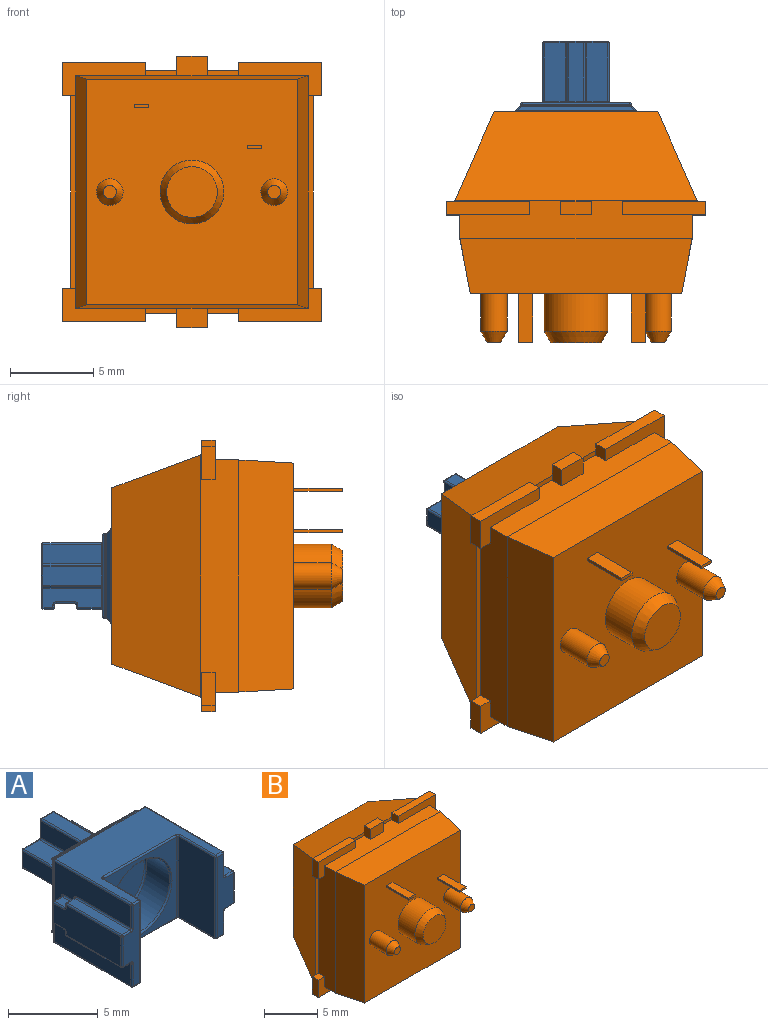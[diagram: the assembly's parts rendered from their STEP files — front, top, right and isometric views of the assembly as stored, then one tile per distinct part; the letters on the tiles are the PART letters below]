
ASSEMBLY  parts=2 mates=1
PART A: 279 faces, bbox 8.9x10.4x5.7 mm
  f0: plane 7.1x6.06mm, normal (0,0,1), area 24.7mm2, adj f124,f129,f136,f137,f148,f155,f161,f168
  f1: plane 3.5x1.15mm, normal (1,0,0), area 3.5mm2, adj f228,f239,f240,f248,f249,f263,f264,f273
  f2: plane 1.4x0.9mm, normal (0,0,-1), area 1.3mm2, adj f250,f251,f264,f265
  f3: plane 0.9x0.6mm, normal (0,0,-1), area 0.5mm2, adj f246,f247,f262,f263
  f4: plane 3.5x1.15mm, normal (-1,0,0), area 3.5mm2, adj f219,f220,f225,f226,f230,f232,f245,f246
  f5: plane 6.06x5.5mm, normal (-1,0,0), area 20.6mm2, adj f61,f68,f69,f79,f88,f89,f100,f112
  f6: plane 5.7x5.5mm, normal (0,-1,0), area 11.7mm2, adj f101,f114,f123,f124,f198
  f7: plane 6.5x4.9mm, normal (0,1,0), area 22.1mm2, adj f163,f172,f173,f174,f205,f206,f210,f211
  f8: plane 6.06x5.5mm, normal (1,0,0), area 20.6mm2, adj f63,f73,f74,f83,f93,f94,f103,f117
  f9: plane 7.1x6.06mm, normal (0,0,-1), area 24.7mm2, adj f101,f106,f107,f121,f122,f142,f143,f157
  f10: cylinder r=2.4mm len=4.8mm, axis (0,-1,0), area 27.1mm2, adj f197,f198
  f11: plane 4.6x4.6mm, normal (0,-1,0), area 16.6mm2, adj f197
  f12: plane 4.9x0.06mm, normal (1,0,0), area 0.3mm2, adj f174,f175,f191,f192
  f13: plane 6.5x0.06mm, normal (0,0,-1), area 0.4mm2, adj f163,f171,f175,f177
  f14: plane 4.9x0.06mm, normal (-1,0,0), area 0.3mm2, adj f171,f172,f189,f190
  f15: plane 6.5x0.06mm, normal (0,0,1), area 0.4mm2, adj f173,f190,f191,f196
  f16: plane 3.5x1.25mm, normal (0,0,-1), area 4.4mm2, adj f267,f272,f275,f278
  f17: plane 3.5x1.25mm, normal (0,0,-1), area 4.4mm2, adj f214,f231,f232,f233
  f18: plane 3.5x1.1mm, normal (-1,0,0), area 3.9mm2, adj f204,f213,f214,f215
  f19: plane 3.5x1.25mm, normal (0,0,1), area 4.4mm2, adj f199,f203,f204,f205
  f20: plane 3.5x1.15mm, normal (-1,0,0), area 4mm2, adj f199,f202,f206,f207
  f21: plane 3.5x0.9mm, normal (0,0,1), area 3.1mm2, adj f207,f212,f216,f217
  f22: plane 3.5x1.15mm, normal (1,0,0), area 4mm2, adj f217,f224,f234,f235
  f23: plane 3.5x1.25mm, normal (0,0,1), area 4.4mm2, adj f235,f244,f253,f254
  f24: plane 3.5x1.1mm, normal (1,0,0), area 3.9mm2, adj f254,f261,f266,f267
  f25: plane 3.8x3.8mm, normal (0,1,0), area 6.6mm2, adj f200,f202,f203,f212,f213,f224,f231,f236
  f26: plane 7.1x0.24mm, normal (0,0.71,0.71), area 2.3mm2, adj f181,f188,f193,f196
  f27: plane 5.5x0.24mm, normal (0.71,0.71,0), area 1.8mm2, adj f178,f179,f192,f193
  f28: plane 5.5x0.24mm, normal (-0.71,0.71,0), area 1.8mm2, adj f169,f176,f188,f189
  f29: plane 7.1x0.24mm, normal (0,0.71,-0.71), area 2.3mm2, adj f158,f176,f177,f178
  f30: plane 5.5x2.8mm, normal (-1,0,0), area 15.4mm2, adj f122,f123,f147,f148
  f31: plane 5.5x1.3mm, normal (0,-1,0), area 4.4mm2, adj f116,f130,f131,f143,f144,f146,f147,f153
  f32: plane 5.5x2.8mm, normal (1,0,0), area 15.4mm2, adj f114,f121,f137,f138
  f33: plane 5.5x1.3mm, normal (0,-1,0), area 4.4mm2, adj f109,f125,f128,f138,f139,f141,f142,f150
  f34: plane 4.3x0.6mm, normal (0,0,1), area 2.6mm2, adj f110,f111,f139,f140
  f35: plane 0.6x0.18mm, normal (0,1,0), area 0.1mm2, adj f86,f87,f111,f112
  f36: plane 0.8x0.6mm, normal (0,0,1), area 0.5mm2, adj f66,f67,f87,f88
  f37: plane 1.3x0.6mm, normal (0,1,0), area 0.8mm2, adj f54,f55,f67,f68
  f38: plane 0.8x0.6mm, normal (0,0,-1), area 0.5mm2, adj f55,f59,f69,f70
  f39: plane 0.6x0.18mm, normal (0,1,0), area 0.1mm2, adj f70,f77,f89,f90
  f40: plane 4.3x0.6mm, normal (0,0,-1), area 2.6mm2, adj f90,f97,f113,f125
  f41: plane 5.3x2.05mm, normal (-1,0,0), area 10.1mm2, adj f54,f59,f65,f66,f77,f78,f86,f97
  f42: plane 4.3x0.6mm, normal (0,0,1), area 2.6mm2, adj f119,f120,f145,f146
  f43: plane 4.3x0.6mm, normal (0,0,-1), area 2.6mm2, adj f92,f102,f116,f117
  f44: plane 0.6x0.18mm, normal (0,1,0), area 0.1mm2, adj f72,f81,f92,f93
  f45: plane 0.8x0.6mm, normal (0,0,-1), area 0.5mm2, adj f57,f62,f72,f73
  f46: plane 1.3x0.6mm, normal (0,1,0), area 0.8mm2, adj f57,f58,f74,f75
  f47: plane 0.8x0.6mm, normal (0,0,1), area 0.5mm2, adj f75,f76,f94,f95
  f48: plane 0.6x0.18mm, normal (0,1,0), area 0.1mm2, adj f95,f96,f118,f119
  f49: plane 5.3x2.05mm, normal (1,0,0), area 10.1mm2, adj f58,f62,f71,f76,f81,f84,f96,f102
  f50: plane 0.9x0.15mm, normal (0,1,0), area 0.1mm2, adj f229,f230,f249,f250
  f51: plane 0.9x0.15mm, normal (0,-1,0), area 0.1mm2, adj f226,f227,f247,f248
  f52: plane 1.1x0.9mm, normal (0,0,-1), area 1mm2, adj f219,f227,f228,f229
  f53: sphere r=0.1mm, area 0mm2, adj f54,f55,f59
  f54: cylinder r=0.1mm len=1.3mm, axis (0,0,1), area 0.2mm2, adj f37,f41,f53,f60
  f55: cylinder r=0.1mm len=0.6mm, axis (1,0,0), area 0.1mm2, adj f37,f38,f53,f61
  f56: sphere r=0.1mm, area 0mm2, adj f57,f58,f62
  f57: cylinder r=0.1mm len=0.6mm, axis (-1,0,0), area 0.1mm2, adj f45,f46,f56,f63
  f58: cylinder r=0.1mm len=1.3mm, axis (0,0,-1), area 0.2mm2, adj f46,f49,f56,f64
  f59: cylinder r=0.1mm len=0.8mm, axis (0,1,0), area 0.1mm2, adj f38,f41,f53,f65
  f60: sphere r=0.1mm, area 0mm2, adj f54,f66,f67
  f61: torus R=0.2mm, axis (1,0,0), area 0mm2, adj f5,f55,f68,f69
  f62: cylinder r=0.1mm len=0.8mm, axis (0,-1,0), area 0.1mm2, adj f45,f49,f56,f71
  f63: torus R=0.2mm, axis (-1,0,0), area 0mm2, adj f8,f57,f73,f74
  f64: sphere r=0.1mm, area 0mm2, adj f58,f75,f76
  f65: torus R=0.2mm, axis (-1,0,0), area 0mm2, adj f41,f59,f70,f77
  f66: cylinder r=0.1mm len=0.8mm, axis (0,-1,0), area 0.1mm2, adj f36,f41,f60,f78
  f67: cylinder r=0.1mm len=0.6mm, axis (1,0,0), area 0.1mm2, adj f36,f37,f60,f79
  f68: cylinder r=0.1mm len=1.3mm, axis (0,0,1), area 0.2mm2, adj f5,f37,f61,f79
  f69: cylinder r=0.1mm len=0.8mm, axis (0,1,0), area 0.1mm2, adj f5,f38,f61,f80
  f70: cylinder r=0.1mm len=0.6mm, axis (-1,0,0), area 0.1mm2, adj f38,f39,f65,f80
  f71: torus R=0.2mm, axis (1,0,0), area 0mm2, adj f49,f62,f72,f81
  f72: cylinder r=0.1mm len=0.6mm, axis (1,0,0), area 0.1mm2, adj f44,f45,f71,f82
  f73: cylinder r=0.1mm len=0.8mm, axis (0,-1,0), area 0.1mm2, adj f8,f45,f63,f82
  f74: cylinder r=0.1mm len=1.3mm, axis (0,0,-1), area 0.2mm2, adj f8,f46,f63,f83
  f75: cylinder r=0.1mm len=0.6mm, axis (-1,0,0), area 0.1mm2, adj f46,f47,f64,f83
  f76: cylinder r=0.1mm len=0.8mm, axis (0,1,0), area 0.1mm2, adj f47,f49,f64,f84
  f77: cylinder r=0.1mm len=0.18mm, axis (0,0,1), area 0mm2, adj f39,f41,f65,f85
  f78: torus R=0.2mm, axis (-1,0,0), area 0mm2, adj f41,f66,f86,f87
  f79: torus R=0.2mm, axis (1,0,0), area 0mm2, adj f5,f67,f68,f88
  f80: sphere r=0.1mm, area 0mm2, adj f69,f70,f89
  f81: cylinder r=0.1mm len=0.18mm, axis (0,0,-1), area 0mm2, adj f44,f49,f71,f91
  f82: sphere r=0.1mm, area 0mm2, adj f72,f73,f93
  f83: torus R=0.2mm, axis (-1,0,0), area 0mm2, adj f8,f74,f75,f94
  f84: torus R=0.2mm, axis (1,0,0), area 0mm2, adj f49,f76,f95,f96
  f85: sphere r=0.1mm, area 0mm2, adj f77,f90,f97
  f86: cylinder r=0.1mm len=0.18mm, axis (0,0,1), area 0mm2, adj f35,f41,f78,f98
  f87: cylinder r=0.1mm len=0.6mm, axis (-1,0,0), area 0.1mm2, adj f35,f36,f78,f99
  f88: cylinder r=0.1mm len=0.8mm, axis (0,-1,0), area 0.1mm2, adj f5,f36,f79,f99
  f89: cylinder r=0.1mm len=0.18mm, axis (0,0,1), area 0mm2, adj f5,f39,f80,f100
  f90: cylinder r=0.1mm len=0.6mm, axis (1,0,0), area 0.1mm2, adj f39,f40,f85,f100
  f91: sphere r=0.1mm, area 0mm2, adj f81,f92,f102
  f92: cylinder r=0.1mm len=0.6mm, axis (-1,0,0), area 0.1mm2, adj f43,f44,f91,f103
  f93: cylinder r=0.1mm len=0.18mm, axis (0,0,-1), area 0mm2, adj f8,f44,f82,f103
  f94: cylinder r=0.1mm len=0.8mm, axis (0,1,0), area 0.1mm2, adj f8,f47,f83,f104
  f95: cylinder r=0.1mm len=0.6mm, axis (1,0,0), area 0.1mm2, adj f47,f48,f84,f104
  f96: cylinder r=0.1mm len=0.18mm, axis (0,0,-1), area 0mm2, adj f48,f49,f84,f105
  f97: cylinder r=0.1mm len=4.3mm, axis (0,1,0), area 0.7mm2, adj f40,f41,f85,f108
  f98: sphere r=0.1mm, area 0mm2, adj f86,f110,f111
  f99: sphere r=0.1mm, area 0mm2, adj f87,f88,f112
  f100: torus R=0.2mm, axis (1,0,0), area 0mm2, adj f5,f89,f90,f113
  f101: cylinder r=0.1mm len=5.7mm, axis (-1,0,0), area 0.9mm2, adj f6,f9,f106,f107
  f102: cylinder r=0.1mm len=4.3mm, axis (0,-1,0), area 0.7mm2, adj f43,f49,f91,f115
  f103: torus R=0.2mm, axis (-1,0,0), area 0mm2, adj f8,f92,f93,f117
  f104: sphere r=0.1mm, area 0mm2, adj f94,f95,f118
  f105: sphere r=0.1mm, area 0mm2, adj f96,f119,f120
  f106: torus R=0.2mm, axis (0,0,1), area 0mm2, adj f9,f101,f114,f121
  f107: torus R=0.2mm, axis (0,0,1), area 0mm2, adj f9,f101,f122,f123
  f108: sphere r=0.1mm, area 0mm2, adj f97,f109,f125
  f109: cylinder r=0.1mm len=2.05mm, axis (0,0,-1), area 0.3mm2, adj f33,f41,f108,f126
  f110: cylinder r=0.1mm len=4.3mm, axis (0,-1,0), area 0.7mm2, adj f34,f41,f98,f126
  f111: cylinder r=0.1mm len=0.6mm, axis (1,0,0), area 0.1mm2, adj f34,f35,f98,f127
  f112: cylinder r=0.1mm len=0.18mm, axis (0,0,1), area 0mm2, adj f5,f35,f99,f127
  f113: cylinder r=0.1mm len=4.3mm, axis (0,1,0), area 0.7mm2, adj f5,f40,f100,f128
  f114: cylinder r=0.1mm len=5.5mm, axis (0,0,-1), area 0.9mm2, adj f6,f32,f106,f129
  f115: sphere r=0.1mm, area 0mm2, adj f102,f116,f130
  f116: cylinder r=0.1mm len=0.6mm, axis (1,0,0), area 0.1mm2, adj f31,f43,f115,f131
  f117: cylinder r=0.1mm len=4.3mm, axis (0,-1,0), area 0.7mm2, adj f8,f43,f103,f131
  f118: cylinder r=0.1mm len=0.18mm, axis (0,0,-1), area 0mm2, adj f8,f48,f104,f132
  f119: cylinder r=0.1mm len=0.6mm, axis (-1,0,0), area 0.1mm2, adj f42,f48,f105,f132
  f120: cylinder r=0.1mm len=4.3mm, axis (0,1,0), area 0.7mm2, adj f42,f49,f105,f133
  f121: cylinder r=0.1mm len=2.8mm, axis (0,1,0), area 0.4mm2, adj f9,f32,f106,f134
  f122: cylinder r=0.1mm len=2.8mm, axis (0,1,0), area 0.4mm2, adj f9,f30,f107,f135
  f123: cylinder r=0.1mm len=5.5mm, axis (0,0,1), area 0.9mm2, adj f6,f30,f107,f136
  f124: cylinder r=0.1mm len=5.7mm, axis (1,0,0), area 0.9mm2, adj f0,f6,f129,f136
  f125: cylinder r=0.1mm len=0.6mm, axis (1,0,0), area 0.1mm2, adj f33,f40,f108,f128
  f126: sphere r=0.1mm, area 0mm2, adj f109,f110,f139
  f127: torus R=0.2mm, axis (1,0,0), area 0mm2, adj f5,f111,f112,f140
  f128: torus R=0.2mm, axis (0,1,0), area 0mm2, adj f33,f113,f125,f141
  f129: torus R=0.2mm, axis (0,0,-1), area 0mm2, adj f0,f114,f124,f137
  f130: cylinder r=0.1mm len=2.05mm, axis (0,0,-1), area 0.3mm2, adj f31,f49,f115,f133
  f131: torus R=0.2mm, axis (0,1,0), area 0mm2, adj f31,f116,f117,f144
  f132: torus R=0.2mm, axis (-1,0,0), area 0mm2, adj f8,f118,f119,f145
  f133: sphere r=0.1mm, area 0mm2, adj f120,f130,f146
  f134: sphere r=0.1mm, area 0mm2, adj f121,f138,f142
  f135: sphere r=0.1mm, area 0mm2, adj f122,f143,f147
  f136: torus R=0.2mm, axis (0,0,-1), area 0mm2, adj f0,f123,f124,f148
  f137: cylinder r=0.1mm len=2.8mm, axis (0,1,0), area 0.4mm2, adj f0,f32,f129,f149
  f138: cylinder r=0.1mm len=5.5mm, axis (0,0,1), area 0.9mm2, adj f32,f33,f134,f149
  f139: cylinder r=0.1mm len=0.6mm, axis (1,0,0), area 0.1mm2, adj f33,f34,f126,f150
  f140: cylinder r=0.1mm len=4.3mm, axis (0,-1,0), area 0.7mm2, adj f5,f34,f127,f150
  f141: cylinder r=0.1mm len=1.53mm, axis (0,0,-1), area 0.2mm2, adj f5,f33,f128,f151
  f142: cylinder r=0.1mm len=0.5mm, axis (1,0,0), area 0.1mm2, adj f9,f33,f134,f151
  f143: cylinder r=0.1mm len=0.5mm, axis (1,0,0), area 0.1mm2, adj f9,f31,f135,f152
  f144: cylinder r=0.1mm len=1.53mm, axis (0,0,1), area 0.2mm2, adj f8,f31,f131,f152
  f145: cylinder r=0.1mm len=4.3mm, axis (0,1,0), area 0.7mm2, adj f8,f42,f132,f153
  f146: cylinder r=0.1mm len=0.6mm, axis (1,0,0), area 0.1mm2, adj f31,f42,f133,f153
  f147: cylinder r=0.1mm len=5.5mm, axis (0,0,-1), area 0.9mm2, adj f30,f31,f135,f154
  f148: cylinder r=0.1mm len=2.8mm, axis (0,1,0), area 0.4mm2, adj f0,f30,f136,f154
  f149: sphere r=0.1mm, area 0mm2, adj f137,f138,f155
  f150: torus R=0.2mm, axis (0,1,0), area 0mm2, adj f33,f139,f140,f156
  f151: sphere r=0.1mm, area 0mm2, adj f141,f142,f157
  f152: sphere r=0.1mm, area 0mm2, adj f143,f144,f159
  f153: torus R=0.2mm, axis (0,1,0), area 0mm2, adj f31,f145,f146,f160
  f154: sphere r=0.1mm, area 0mm2, adj f147,f148,f161
  f155: cylinder r=0.1mm len=0.5mm, axis (-1,0,0), area 0.1mm2, adj f0,f33,f149,f162
  f156: cylinder r=0.1mm len=1.53mm, axis (0,0,-1), area 0.2mm2, adj f5,f33,f150,f162
  f157: cylinder r=0.1mm len=6.06mm, axis (0,-1,0), area 1mm2, adj f5,f9,f151,f165
  f158: cylinder r=0.1mm len=7.1mm, axis (-1,0,0), area 0.6mm2, adj f9,f29,f165,f166
  f159: cylinder r=0.1mm len=6.06mm, axis (0,-1,0), area 1mm2, adj f8,f9,f152,f166
  f160: cylinder r=0.1mm len=1.53mm, axis (0,0,1), area 0.2mm2, adj f8,f31,f153,f167
  f161: cylinder r=0.1mm len=0.5mm, axis (-1,0,0), area 0.1mm2, adj f0,f31,f154,f167
  f162: sphere r=0.1mm, area 0mm2, adj f155,f156,f168
  f163: cylinder r=0.1mm len=6.5mm, axis (1,0,0), area 1mm2, adj f7,f13,f164,f170
  f164: sphere r=0.1mm, area 0mm2, adj f163,f171,f172
  f165: sphere r=0.1mm, area 0mm2, adj f157,f158,f169,f176
  f166: sphere r=0.1mm, area 0mm2, adj f158,f159,f178,f179
  f167: sphere r=0.1mm, area 0mm2, adj f160,f161,f180
  f168: cylinder r=0.1mm len=6.06mm, axis (0,-1,0), area 1mm2, adj f0,f5,f162,f182
  f169: cylinder r=0.1mm len=5.5mm, axis (0,0,1), area 0.4mm2, adj f5,f28,f165,f182
  f170: sphere r=0.1mm, area 0mm2, adj f163,f174,f175
  f171: cylinder r=0.1mm len=0.1mm, axis (0,-1,0), area 0mm2, adj f13,f14,f164,f183
  f172: cylinder r=0.1mm len=4.9mm, axis (0,0,-1), area 0.8mm2, adj f7,f14,f164,f184
  f173: cylinder r=0.1mm len=6.5mm, axis (-1,0,0), area 1mm2, adj f7,f15,f184,f185
  f174: cylinder r=0.1mm len=4.9mm, axis (0,0,1), area 0.8mm2, adj f7,f12,f170,f185
  f175: cylinder r=0.1mm len=0.1mm, axis (0,-1,0), area 0mm2, adj f12,f13,f170,f186
  f176: cylinder r=0.1mm len=0.31mm, axis (0.58,0.58,0.58), area 0mm2, adj f28,f29,f165,f183
  f177: cylinder r=0.1mm len=6.62mm, axis (1,0,0), area 0.5mm2, adj f13,f29,f183,f186
  f178: cylinder r=0.1mm len=0.31mm, axis (0.58,-0.58,-0.58), area 0mm2, adj f27,f29,f166,f186
  f179: cylinder r=0.1mm len=5.5mm, axis (0,0,-1), area 0.4mm2, adj f8,f27,f166,f187
  f180: cylinder r=0.1mm len=6.06mm, axis (0,-1,0), area 1mm2, adj f0,f8,f167,f187
  f181: cylinder r=0.1mm len=7.1mm, axis (1,0,0), area 0.6mm2, adj f0,f26,f182,f187
  f182: sphere r=0.1mm, area 0mm2, adj f168,f169,f181,f188
  f183: bspline ~0.14x0.14mm, area 0mm2, adj f171,f176,f177,f189
  f184: sphere r=0.1mm, area 0mm2, adj f172,f173,f190
  f185: sphere r=0.1mm, area 0mm2, adj f173,f174,f191
  f186: bspline ~0.14x0.14mm, area 0mm2, adj f175,f177,f178,f192
  f187: sphere r=0.1mm, area 0mm2, adj f179,f180,f181,f193
  f188: cylinder r=0.1mm len=0.31mm, axis (0.58,0.58,-0.58), area 0mm2, adj f26,f28,f182,f194
  f189: cylinder r=0.1mm len=5.02mm, axis (0,0,-1), area 0.4mm2, adj f14,f28,f183,f194
  f190: cylinder r=0.1mm len=0.1mm, axis (0,-1,0), area 0mm2, adj f14,f15,f184,f194
  f191: cylinder r=0.1mm len=0.1mm, axis (0,-1,0), area 0mm2, adj f12,f15,f185,f195
  f192: cylinder r=0.1mm len=5.02mm, axis (0,0,1), area 0.4mm2, adj f12,f27,f186,f195
  f193: cylinder r=0.1mm len=0.31mm, axis (0.58,-0.58,0.58), area 0mm2, adj f26,f27,f187,f195
  f194: bspline ~0.14x0.14mm, area 0mm2, adj f188,f189,f190,f196
  f195: bspline ~0.14x0.14mm, area 0mm2, adj f191,f192,f193,f196
  f196: cylinder r=0.1mm len=6.62mm, axis (-1,0,0), area 0.5mm2, adj f15,f26,f194,f195
  f197: torus R=2.3mm, axis (0,-1,0), area 2.3mm2, adj f10,f11
  f198: torus R=2.5mm, axis (0,1,0), area 2.4mm2, adj f6,f10
  f199: cylinder r=0.1mm len=3.5mm, axis (0,1,0), area 0.5mm2, adj f19,f20,f200,f201
  f200: torus R=0.2mm, axis (0,-1,0), area 0mm2, adj f25,f199,f202,f203
  f201: sphere r=0.1mm, area 0mm2, adj f199,f205,f206
  f202: cylinder r=0.1mm len=1.15mm, axis (0,0,1), area 0.2mm2, adj f20,f25,f200,f208
  f203: cylinder r=0.1mm len=1.25mm, axis (1,0,0), area 0.2mm2, adj f19,f25,f200,f209
  f204: cylinder r=0.1mm len=3.5mm, axis (0,-1,0), area 0.5mm2, adj f18,f19,f209,f210
  f205: cylinder r=0.1mm len=1.25mm, axis (1,0,0), area 0.2mm2, adj f7,f19,f201,f210
  f206: cylinder r=0.1mm len=1.15mm, axis (0,0,1), area 0.2mm2, adj f7,f20,f201,f211
  f207: cylinder r=0.1mm len=3.5mm, axis (0,-1,0), area 0.5mm2, adj f20,f21,f208,f211
  f208: sphere r=0.1mm, area 0mm2, adj f202,f207,f212
  f209: sphere r=0.1mm, area 0mm2, adj f203,f204,f213
  f210: torus R=0.2mm, axis (0,1,0), area 0mm2, adj f7,f204,f205,f215
  f211: torus R=0.2mm, axis (0,1,0), area 0mm2, adj f7,f206,f207,f216
  f212: cylinder r=0.1mm len=0.9mm, axis (1,0,0), area 0.1mm2, adj f21,f25,f208,f218
  f213: cylinder r=0.1mm len=1.1mm, axis (0,0,1), area 0.2mm2, adj f18,f25,f209,f221
  f214: cylinder r=0.1mm len=3.5mm, axis (0,-1,0), area 0.5mm2, adj f17,f18,f221,f222
  f215: cylinder r=0.1mm len=1.1mm, axis (0,0,1), area 0.2mm2, adj f7,f18,f210,f222
  f216: cylinder r=0.1mm len=0.9mm, axis (1,0,0), area 0.1mm2, adj f7,f21,f211,f223
  f217: cylinder r=0.1mm len=3.5mm, axis (0,-1,0), area 0.5mm2, adj f21,f22,f218,f223
  f218: sphere r=0.1mm, area 0mm2, adj f212,f217,f224
  f219: cylinder r=0.1mm len=1.1mm, axis (0,-1,0), area 0.2mm2, adj f4,f52,f220,f225
  f220: torus R=0.2mm, axis (1,0,0), area 0mm2, adj f4,f219,f226,f227
  f221: sphere r=0.1mm, area 0mm2, adj f213,f214,f231
  f222: torus R=0.2mm, axis (0,1,0), area 0mm2, adj f7,f214,f215,f233
  f223: torus R=0.2mm, axis (0,1,0), area 0mm2, adj f7,f216,f217,f234
  f224: cylinder r=0.1mm len=1.15mm, axis (0,0,-1), area 0.2mm2, adj f22,f25,f218,f236
  f225: torus R=0.2mm, axis (1,0,0), area 0mm2, adj f4,f219,f229,f230
  f226: cylinder r=0.1mm len=0.15mm, axis (0,0,1), area 0mm2, adj f4,f51,f220,f238
  f227: cylinder r=0.1mm len=0.9mm, axis (-1,0,0), area 0.1mm2, adj f51,f52,f220,f239
  f228: cylinder r=0.1mm len=1.1mm, axis (0,1,0), area 0.2mm2, adj f1,f52,f239,f240
  f229: cylinder r=0.1mm len=0.9mm, axis (1,0,0), area 0.1mm2, adj f50,f52,f225,f240
  f230: cylinder r=0.1mm len=0.15mm, axis (0,0,1), area 0mm2, adj f4,f50,f225,f241
  f231: cylinder r=0.1mm len=1.25mm, axis (-1,0,0), area 0.2mm2, adj f17,f25,f221,f237
  f232: cylinder r=0.1mm len=3.5mm, axis (0,1,0), area 0.5mm2, adj f4,f17,f237,f242
  f233: cylinder r=0.1mm len=1.25mm, axis (-1,0,0), area 0.2mm2, adj f7,f17,f222,f242
  f234: cylinder r=0.1mm len=1.15mm, axis (0,0,-1), area 0.2mm2, adj f7,f22,f223,f243
  f235: cylinder r=0.1mm len=3.5mm, axis (0,1,0), area 0.5mm2, adj f22,f23,f236,f243
  f236: torus R=0.2mm, axis (0,-1,0), area 0mm2, adj f25,f224,f235,f244
  f237: torus R=0.2mm, axis (0,-1,0), area 0mm2, adj f25,f231,f232,f245
  f238: sphere r=0.1mm, area 0mm2, adj f226,f246,f247
  f239: torus R=0.2mm, axis (-1,0,0), area 0mm2, adj f1,f227,f228,f248
  f240: torus R=0.2mm, axis (-1,0,0), area 0mm2, adj f1,f228,f229,f249
  f241: sphere r=0.1mm, area 0mm2, adj f230,f250,f251
  f242: sphere r=0.1mm, area 0mm2, adj f232,f233,f252
  f243: sphere r=0.1mm, area 0mm2, adj f234,f235,f253
  f244: cylinder r=0.1mm len=1.25mm, axis (1,0,0), area 0.2mm2, adj f23,f25,f236,f255
  f245: cylinder r=0.1mm len=1.15mm, axis (0,0,1), area 0.2mm2, adj f4,f25,f237,f256
  f246: cylinder r=0.1mm len=0.6mm, axis (0,-1,0), area 0.1mm2, adj f3,f4,f238,f256
  f247: cylinder r=0.1mm len=0.9mm, axis (1,0,0), area 0.1mm2, adj f3,f51,f238,f257
  f248: cylinder r=0.1mm len=0.15mm, axis (0,0,1), area 0mm2, adj f1,f51,f239,f257
  f249: cylinder r=0.1mm len=0.15mm, axis (0,0,1), area 0mm2, adj f1,f50,f240,f258
  f250: cylinder r=0.1mm len=0.9mm, axis (-1,0,0), area 0.1mm2, adj f2,f50,f241,f258
  f251: cylinder r=0.1mm len=1.4mm, axis (0,-1,0), area 0.2mm2, adj f2,f4,f241,f259
  f252: cylinder r=0.1mm len=1.15mm, axis (0,0,1), area 0.2mm2, adj f4,f7,f242,f259
  f253: cylinder r=0.1mm len=1.25mm, axis (1,0,0), area 0.2mm2, adj f7,f23,f243,f260
  f254: cylinder r=0.1mm len=3.5mm, axis (0,-1,0), area 0.5mm2, adj f23,f24,f255,f260
  f255: sphere r=0.1mm, area 0mm2, adj f244,f254,f261
  f256: sphere r=0.1mm, area 0mm2, adj f245,f246,f262
  f257: sphere r=0.1mm, area 0mm2, adj f247,f248,f263
  f258: sphere r=0.1mm, area 0mm2, adj f249,f250,f264
  f259: torus R=0.2mm, axis (0,1,0), area 0mm2, adj f7,f251,f252,f265
  f260: torus R=0.2mm, axis (0,1,0), area 0mm2, adj f7,f253,f254,f266
  f261: cylinder r=0.1mm len=1.1mm, axis (0,0,-1), area 0.2mm2, adj f24,f25,f255,f268
  f262: cylinder r=0.1mm len=0.9mm, axis (-1,0,0), area 0.1mm2, adj f3,f25,f256,f269
  f263: cylinder r=0.1mm len=0.6mm, axis (0,-1,0), area 0.1mm2, adj f1,f3,f257,f269
  f264: cylinder r=0.1mm len=1.4mm, axis (0,-1,0), area 0.2mm2, adj f1,f2,f258,f270
  f265: cylinder r=0.1mm len=0.9mm, axis (-1,0,0), area 0.1mm2, adj f2,f7,f259,f270
  f266: cylinder r=0.1mm len=1.1mm, axis (0,0,-1), area 0.2mm2, adj f7,f24,f260,f271
  f267: cylinder r=0.1mm len=3.5mm, axis (0,-1,0), area 0.5mm2, adj f16,f24,f268,f271
  f268: sphere r=0.1mm, area 0mm2, adj f261,f267,f272
  f269: sphere r=0.1mm, area 0mm2, adj f262,f263,f273
  f270: torus R=0.2mm, axis (0,1,0), area 0mm2, adj f7,f264,f265,f274
  f271: torus R=0.2mm, axis (0,1,0), area 0mm2, adj f7,f266,f267,f275
  f272: cylinder r=0.1mm len=1.25mm, axis (-1,0,0), area 0.2mm2, adj f16,f25,f268,f276
  f273: cylinder r=0.1mm len=1.15mm, axis (0,0,-1), area 0.2mm2, adj f1,f25,f269,f276
  f274: cylinder r=0.1mm len=1.15mm, axis (0,0,-1), area 0.2mm2, adj f1,f7,f270,f277
  f275: cylinder r=0.1mm len=1.25mm, axis (-1,0,0), area 0.2mm2, adj f7,f16,f271,f277
  f276: torus R=0.2mm, axis (0,-1,0), area 0mm2, adj f25,f272,f273,f278
  f277: sphere r=0.1mm, area 0mm2, adj f274,f275,f278
  f278: cylinder r=0.1mm len=3.5mm, axis (0,1,0), area 0.5mm2, adj f1,f16,f276,f277
PART B: 73 faces, bbox 15.6x13.9x16.3 mm
  f0: plane 10.62x9.87mm, normal (0,1,0), area 63.2mm2, adj f5,f6,f7,f8,f68,f69,f70,f71
  f1: plane 13.98x2.3mm, normal (0,0,1), area 23.8mm2, adj f2,f4,f9,f23,f31,f32,f34,f54
  f2: plane 13.98x2.3mm, normal (-1,0,0), area 30.2mm2, adj f1,f3,f9,f24,f48,f49,f50,f54
  f3: plane 13.98x2.3mm, normal (0,0,-1), area 23.8mm2, adj f2,f4,f9,f22,f37,f38,f40,f43
  f4: plane 13.98x2.3mm, normal (1,0,0), area 30.2mm2, adj f1,f3,f9,f21,f31,f32,f33,f37
  f5: plane 14.58x5.35mm, normal (0,0.35,-0.94), area 69.7mm2, adj f0,f6,f7,f9
  f6: plane 14.58x5.35mm, normal (0.92,0.4,0), area 73.7mm2, adj f0,f5,f8,f9
  f7: plane 14.58x5.35mm, normal (-0.92,0.4,0), area 73.7mm2, adj f0,f5,f8,f9
  f8: plane 14.58x5.35mm, normal (0,0.35,0.94), area 69.7mm2, adj f0,f6,f7,f9
  f9: plane 14.58x14.58mm, normal (0,-1,0), area 17.1mm2, adj f1,f2,f3,f4,f5,f6,f7,f8
  f10: plane 0.86x0.2mm, normal (0,-1,0), area 0.2mm2, adj f14,f15,f16,f17
  f11: plane 0.8x0.8mm, normal (0,-1,0), area 0.5mm2, adj f66
  f12: plane 3.05x3.05mm, normal (0,-1,0), area 7.3mm2, adj f65
  f13: plane 0.8x0.8mm, normal (0,-1,0), area 0.5mm2, adj f67
  f14: plane 2.95x0.86mm, normal (0,0,-1), area 2.5mm2, adj f10,f15,f17,f26
  f15: plane 2.95x0.2mm, normal (1,0,0), area 0.6mm2, adj f10,f14,f16,f26
  f16: plane 2.95x0.86mm, normal (0,0,1), area 2.5mm2, adj f10,f15,f17,f26
  f17: plane 2.95x0.2mm, normal (-1,0,0), area 0.6mm2, adj f10,f14,f16,f26
  f18: cylinder r=0.8mm len=2.26mm, axis (0,-1,0), area 11.3mm2, adj f26,f66
  f19: cylinder r=1.93mm len=3.85mm, axis (0,-1,0), area 27.3mm2, adj f26,f65
  f20: cylinder r=0.8mm len=2.26mm, axis (0,-1,0), area 11.3mm2, adj f26,f67
  f21: plane 13.98x3.3mm, normal (0.98,-0.18,0), area 46.3mm2, adj f4,f22,f23,f26
  f22: plane 13.98x3.3mm, normal (0,-0.06,-1), area 44.2mm2, adj f3,f21,f24,f26
  f23: plane 13.98x3.3mm, normal (0,-0.06,1), area 44.2mm2, adj f1,f21,f24,f26
  f24: plane 13.98x3.3mm, normal (-0.98,-0.18,0), area 46.3mm2, adj f2,f22,f23,f26
  f25: plane 0.86x0.2mm, normal (0,-1,0), area 0.2mm2, adj f27,f28,f29,f30
  f26: plane 13.6x12.74mm, normal (0,-1,0), area 157.3mm2, adj f14,f15,f16,f17,f18,f19,f20,f21
  f27: plane 2.95x0.86mm, normal (0,0,-1), area 2.5mm2, adj f25,f26,f28,f30
  f28: plane 2.95x0.2mm, normal (1,0,0), area 0.6mm2, adj f25,f26,f27,f29
  f29: plane 2.95x0.86mm, normal (0,0,1), area 2.5mm2, adj f25,f26,f28,f30
  f30: plane 2.95x0.2mm, normal (-1,0,0), area 0.6mm2, adj f25,f26,f27,f29
  f31: plane 5x2mm, normal (0,-1,0), area 5.1mm2, adj f1,f4,f33,f34,f35,f36
  f32: plane 5x2mm, normal (0,1,0), area 5.1mm2, adj f1,f4,f33,f34,f35,f36
  f33: plane 0.83x0.82mm, normal (0,0,-1), area 0.7mm2, adj f4,f31,f32,f36
  f34: plane 0.83x0.82mm, normal (-1,0,0), area 0.7mm2, adj f1,f31,f32,f35
  f35: plane 5x0.82mm, normal (0,0,1), area 4.1mm2, adj f31,f32,f34,f36
  f36: plane 2x0.82mm, normal (1,0,0), area 1.6mm2, adj f31,f32,f33,f35
  f37: plane 5x2mm, normal (0,-1,0), area 5.1mm2, adj f3,f4,f39,f40,f41,f42
  f38: plane 5x2mm, normal (0,1,0), area 5.1mm2, adj f3,f4,f39,f40,f41,f42
  f39: plane 0.83x0.82mm, normal (0,0,1), area 0.7mm2, adj f4,f37,f38,f42
  f40: plane 0.83x0.82mm, normal (-1,0,0), area 0.7mm2, adj f3,f37,f38,f41
  f41: plane 5x0.82mm, normal (0,0,-1), area 4.1mm2, adj f37,f38,f40,f42
  f42: plane 2x0.82mm, normal (1,0,0), area 1.6mm2, adj f37,f38,f39,f41
  f43: plane 1.82x1.18mm, normal (0,-1,0), area 2.1mm2, adj f3,f45,f46,f47
  f44: plane 1.82x1.18mm, normal (0,1,0), area 2.1mm2, adj f3,f45,f46,f47
  f45: plane 1.18x0.82mm, normal (-1,0,0), area 1mm2, adj f3,f43,f44,f46
  f46: plane 1.82x0.82mm, normal (0,0,-1), area 1.5mm2, adj f43,f44,f45,f47
  f47: plane 1.18x0.82mm, normal (1,0,0), area 1mm2, adj f3,f43,f44,f46
  f48: plane 5x2mm, normal (0,-1,0), area 5.1mm2, adj f2,f3,f50,f51,f52,f53
  f49: plane 5x2mm, normal (0,1,0), area 5.1mm2, adj f2,f3,f50,f51,f52,f53
  f50: plane 0.83x0.82mm, normal (0,0,1), area 0.7mm2, adj f2,f48,f49,f53
  f51: plane 0.83x0.82mm, normal (1,0,0), area 0.7mm2, adj f3,f48,f49,f52
  f52: plane 5x0.82mm, normal (0,0,-1), area 4.1mm2, adj f48,f49,f51,f53
  f53: plane 2x0.82mm, normal (-1,0,0), area 1.6mm2, adj f48,f49,f50,f52
  f54: plane 5x2mm, normal (0,-1,0), area 5.1mm2, adj f1,f2,f56,f57,f58,f59
  f55: plane 5x2mm, normal (0,1,0), area 5.1mm2, adj f1,f2,f56,f57,f58,f59
  f56: plane 0.83x0.82mm, normal (0,0,-1), area 0.7mm2, adj f2,f54,f55,f59
  f57: plane 0.83x0.82mm, normal (1,0,0), area 0.7mm2, adj f1,f54,f55,f58
  f58: plane 5x0.82mm, normal (0,0,1), area 4.1mm2, adj f54,f55,f57,f59
  f59: plane 2x0.82mm, normal (-1,0,0), area 1.6mm2, adj f54,f55,f56,f58
  f60: plane 1.82x1.18mm, normal (0,-1,0), area 2.1mm2, adj f1,f62,f63,f64
  f61: plane 1.82x1.18mm, normal (0,1,0), area 2.1mm2, adj f1,f62,f63,f64
  f62: plane 1.18x0.82mm, normal (-1,0,0), area 1mm2, adj f1,f60,f61,f63
  f63: plane 1.82x0.82mm, normal (0,0,1), area 1.5mm2, adj f60,f61,f62,f64
  f64: plane 1.18x0.82mm, normal (1,0,0), area 1mm2, adj f1,f60,f61,f63
  f65: cone r=1.93mm half-angle=30deg, axis (0,1,0), area 8.7mm2, adj f12,f19
  f66: cone r=0.8mm half-angle=30deg, axis (0,1,0), area 3mm2, adj f11,f18
  f67: cone r=0.8mm half-angle=30deg, axis (0,1,0), area 3mm2, adj f13,f20
  f68: plane 8x7.3mm, normal (0,0,-1), area 58.4mm2, adj f0,f69,f71,f72
  f69: plane 8x5.7mm, normal (-1,0,0), area 45.6mm2, adj f0,f68,f70,f72
  f70: plane 8x7.3mm, normal (0,0,1), area 58.4mm2, adj f0,f69,f71,f72
  f71: plane 8x5.7mm, normal (1,0,0), area 45.6mm2, adj f0,f68,f70,f72
  f72: plane 7.3x5.7mm, normal (0,1,0), area 41.6mm2, adj f68,f69,f70,f71
PLACE A t=(0,10.75,0)mm
PLACE B t=(0,8.55,0)mm
MATE slider A.f10 <-> B.f19  axis (0,-1,0) through (0,12.75,0)mm
